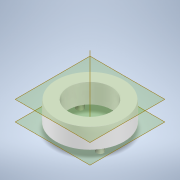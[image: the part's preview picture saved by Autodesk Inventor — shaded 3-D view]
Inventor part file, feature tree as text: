
AUTODESK INVENTOR PART (.ipt)
format: ipt  version: 2021 (Build 250183000, 183)  size: 508,416 bytes
history: native  units: in
note: dims shown in document units (in); Inventor stores cm internally (conversion verified against a paired STEP export)
features: sketch x8, extrude x7, fillet x2, plane x2, other x1, revolve x1, pattern_circular x1, mirror x1, chamfer x1
ambient origin geometry x8: Origin, YZ Plane, XZ Plane, XY Plane, X Axis, Y Axis, Z Axis, Center Point
bodies: Solid1 (feature_tree)
feature tree (24):
  extrude  "Extrusion1"  Depth=1.0236in
  other  "Work Axis1"
  revolve  "Revolution1"  [1 undecoded]
  extrude  "Extrusion2"  Depth=1.0079in
  extrude  "Extrusion3"  TaperAngle=90.0deg  [1 undecoded]
  extrude  "Extrusion4"  Depth=0.8976in
  extrude  "Extrusion5"  Depth=1.0236in TaperAngle=0.0deg
  pattern_circular  "Circular Pattern1"  [2 undecoded]
  mirror  "Mirror1"
  fillet  "Fillet2"  Radius=0.1969in
  extrude  "Extrusion7"  Depth=1.9685in TaperAngle=240.0deg
  chamfer  "Chamfer2"  Distance=0.5039in
  fillet  "Fillet3"  Radius=0.0394in
  plane  "Work Plane4"
  extrude  "Extrusion12"  Depth=0.7079in
  sketch  "Sketch1"  dims[d0=2.0472in d1=1.0236in]
  sketch  "Sketch2"  dims[d2=1.0236in d3=1.0236in]
  sketch  "Sketch3"  dims[d4=1.378in d5=0.0in d6=1.0079in]
  sketch  "Sketch4"  dims[d7=90.0deg d8=90.0deg]
  sketch  "Sketch5"  dims[d9=0.0394in d10=0.0in d11=0.8976in]
  sketch  "Sketch8"  dims[d12=0.0in d13=0.0in d14=1.0236in d15=0.0in]
  sketch  "Sketch10"  dims[d16=1.2913in]
  plane  "Work Plane2"
  sketch  "Sketch15"  dims[d21=0.2126in d22=0.8268in d23=0.1969in d24=0.0in d25=1.9685in d26=240.0deg d33=0.5039in d34=0.0394in d35=0.7079in d36=0.3937in d37=0.3539in d38=0.2362in d39=0.3937in d40=0.0in d41=0.3937in d42=0.2283in d43=45.0deg d44=0.1969in d48=0.0in d56=-0.5906in d57=0.0in d58=0.0in d45=0.0197in d46=0.0344in d47=0.0197in]
note: 4 required parameter values undecoded (feature->parameter linkage not recoverable at this tier; creation-order binding heuristic only, values carry confidence <= 0.55)